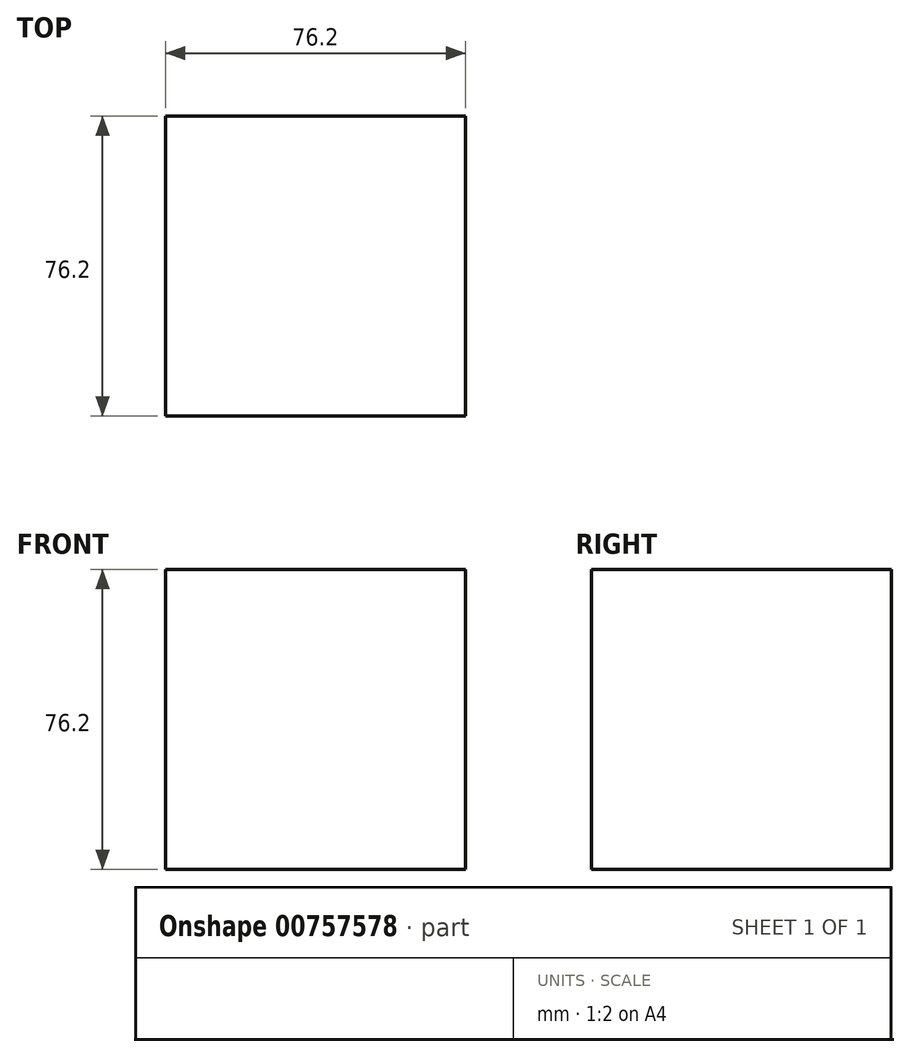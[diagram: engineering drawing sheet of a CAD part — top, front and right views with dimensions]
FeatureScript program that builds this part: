
annotation { "Feature Type Name" : "Feature", "Feature Type Description" : "" }
export const myFeature = defineFeature(function(context is Context, id is Id, definition is map)
    precondition{}
    {
        {
            var Q0;
            Q0=qCreatedBy(makeId("Front.planeOp"),FACE);
            var sketch = newSketch(context, id + "F0", { "sketchPlane" : qUnion([Q0])});
            skLineSegment(sketch, "E0", {"start": v(-44.18, 49.72) * mm, "end": v(32.02, 49.72) * mm});
            skLineSegment(sketch, "E1", {"start": v(32.02, 49.72) * mm, "end": v(32.02, -26.48) * mm});
            skLineSegment(sketch, "E2", {"start": v(32.02, -26.48) * mm, "end": v(-44.18, -26.48) * mm});
            skLineSegment(sketch, "E3", {"start": v(-44.18, -26.48) * mm, "end": v(-44.18, 49.72) * mm});
            skSolve(sketch);
        }
        {
            var Q0;
            Q0=makeQuery(id+"F0.imprint","IMPRINT",FACE,{"disambiguationData":[TD([[makeQuery(id+"F0.imprint","IMPRINT",EDGE,{"derivedFrom":sQuery(id+"F0.wireOp",EDGE,"E0")}),-1.0]])]});
            extrude(context, id + "F1", {"entities" : qUnion([Q0]), "depth" : 76.2 * mm, "offsetDistance" : 25.4 * mm});
        }
    });
